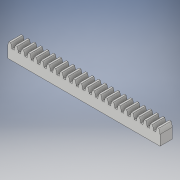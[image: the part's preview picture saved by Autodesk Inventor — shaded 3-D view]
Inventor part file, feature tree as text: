
AUTODESK INVENTOR PART (.ipt)
format: ipt  version: 2019 (Build 230136000, 136)  size: 195,072 bytes
history: native  units: mm
features: extrude x2, sketch x2, pattern_linear x1, projected_geometry x1
ambient origin geometry x8: Origin, YZ Plane, XZ Plane, XY Plane, X Axis, Y Axis, Z Axis, Center Point
bodies: Solid1 (feature_tree)
feature tree (6):
  extrude  "Extrusion1"  Depth=10.0mm
  extrude  "Extrusion2"  Depth=16.578504mm
  pattern_linear  "Rectangular Pattern1"  Spacing1=16.578504mm  [1 undecoded]
  sketch  "Sketch1"  dims[d0=148.627mm d1=10.0mm]
  sketch  "Sketch2"  dims[d2=12.0mm d3=0.0mm d4=16.578504mm d5=16.578504mm d6=22.0mm d7=28.84419mm d8=1.193189mm d9=6.418005mm d10=4.604341mm d11=1.193189mm d12=12.0mm d13=0.0mm d14=240.0mm d16=6.28318mm]
  projected_geometry  "Projected Loop1"
note: 1 required parameter value undecoded (feature->parameter linkage not recoverable at this tier; creation-order binding heuristic only, values carry confidence <= 0.55)
